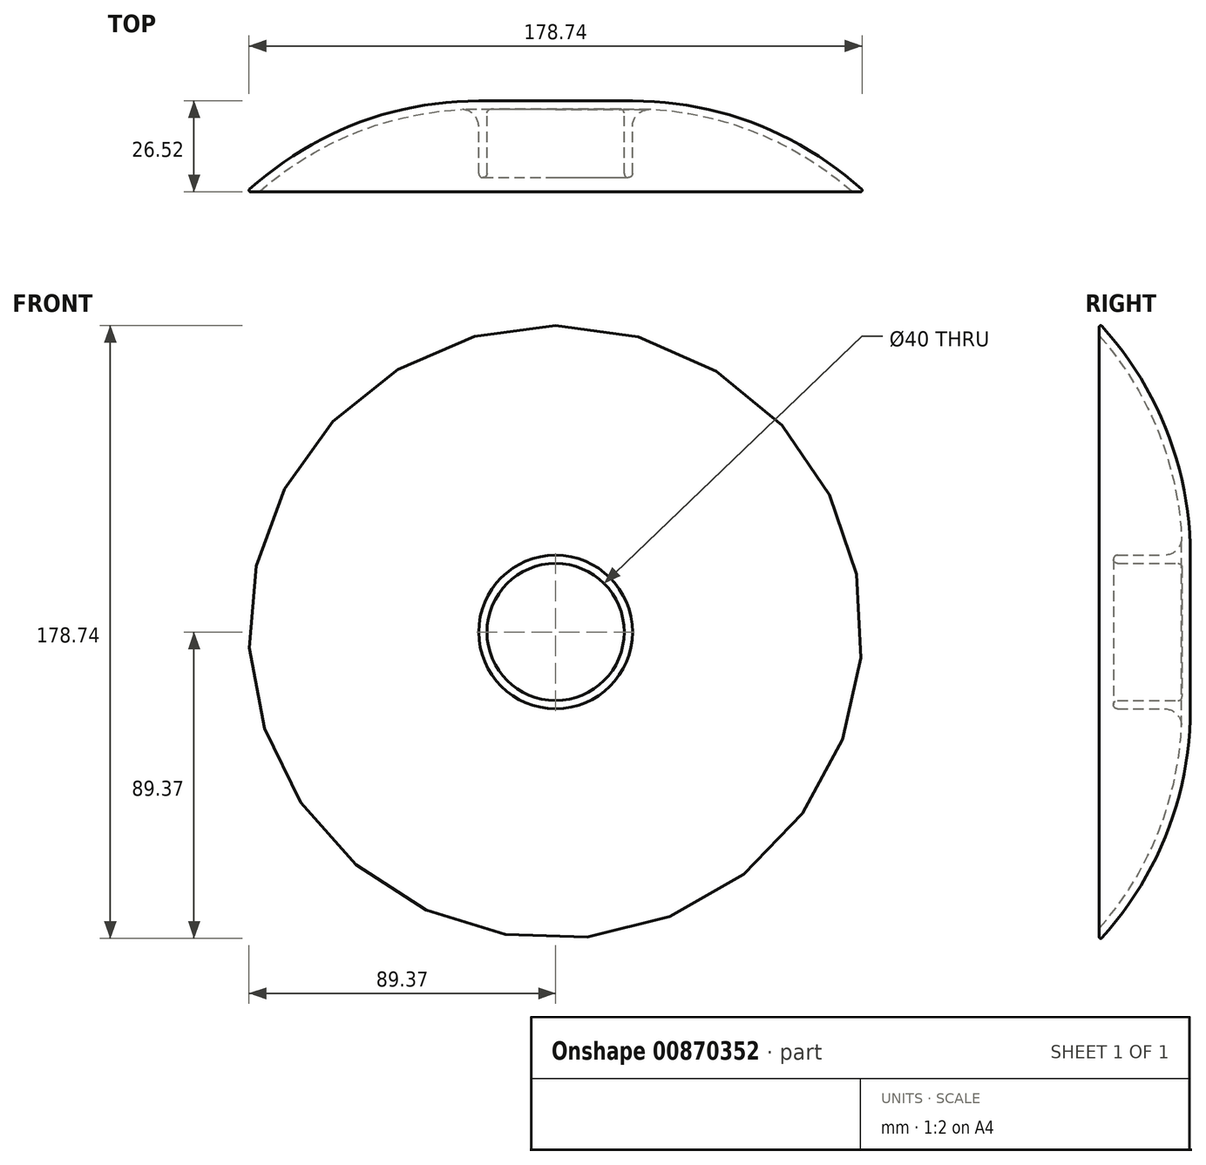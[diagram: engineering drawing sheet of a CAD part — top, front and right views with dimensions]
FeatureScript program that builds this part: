
annotation { "Feature Type Name" : "Feature", "Feature Type Description" : "" }
export const myFeature = defineFeature(function(context is Context, id is Id, definition is map)
    precondition{}
    {
        {
            var Q0;
            Q0=qCreatedBy(makeId("Top.planeOp"),FACE);
            var sketch = newSketch(context, id + "F0", { "sketchPlane" : qUnion([Q0])});
            skLineSegment(sketch, "E0.bottom", {"start": v(0, 32.73) * mm, "end": v(22.4, 32.73) * mm});
            skLineSegment(sketch, "E0.top", {"start": v(0, 30.33) * mm, "end": v(20, 30.33) * mm});
            skArc(sketch, "E1", {"start": v(22.4, 30.33) * mm, "mid": v(56.6, 24.1) * mm, "end": v(86.42, 6.2) * mm});
            skArc(sketch, "E2.0", {"start": v(22.4, 32.73) * mm, "mid": v(58.7, 25.86) * mm, "end": v(90, 6.2) * mm});
            skLineSegment(sketch, "E3", {"start": v(86.42, 6.2) * mm, "end": v(90, 6.2) * mm});
            skLineSegment(sketch, "E4.top", {"start": v(22.4, 10.33) * mm, "end": v(20, 10.33) * mm});
            skLineSegment(sketch, "E4.left", {"start": v(22.4, 30.33) * mm, "end": v(22.4, 10.33) * mm});
            skLineSegment(sketch, "E4.right", {"start": v(20, 30.33) * mm, "end": v(20, 10.33) * mm});
            skLineSegment(sketch, "E5", {"start": v(0, 47.87) * mm, "end": v(0, 16.24) * mm, "construction": true});
            skLineSegment(sketch, "E6", {"start": v(0, 32.73) * mm, "end": v(0, 30.33) * mm});
            skSolve(sketch);
        }
        {
            var Q0;
            Q0 = qSketchRegion(id + "F0", true);
            var Q1;
            Q1=sQuery(id+"F0.wireOp",EDGE,"E5");
            revolve(context, id + "F1", {"surfaceOperationType" : NewSurfaceOperationType.NEW, "entities" : qUnion([Q0]), "axis" : qUnion([Q1]), "revolveType" : RevolveType.FULL});
        }
        {
            var Q0;
            Q0=makeQuery(id+"F1.opRevolve","SWEPT_EDGE",EDGE,{"disambiguationData":[OSD([sQuery(id+"F0.wireOp",EDGE,"E1"),sQuery(id+"F0.wireOp",EDGE,"E4.left")])]});
            fillet(context, id + "F2", {"entities" : qUnion([Q0]), "radius" : 5 * mm, "tangentPropagation" : true, "allowEdgeOverflow" : false});
        }
        {
            var Q0;
            Q0=makeQuery(id+"F1.opRevolve","SWEPT_EDGE",EDGE,{"disambiguationData":[OSD([sQuery(id+"F0.wireOp",EDGE,"E0.top"),sQuery(id+"F0.wireOp",EDGE,"E4.right")])]});
            fillet(context, id + "F3", {"entities" : qUnion([Q0]), "radius" : 1.2 * mm, "tangentPropagation" : true, "allowEdgeOverflow" : false});
        }
        {
            var Q0;
            Q0=makeQuery(id+"F1.opRevolve","SWEPT_EDGE",EDGE,{"disambiguationData":[OSD([sQuery(id+"F0.wireOp",EDGE,"E4.top"),sQuery(id+"F0.wireOp",EDGE,"E4.right")])]});
            var Q1;
            Q1=makeQuery(id+"F1.opRevolve","SWEPT_EDGE",EDGE,{"disambiguationData":[OSD([sQuery(id+"F0.wireOp",EDGE,"E4.top"),sQuery(id+"F0.wireOp",EDGE,"E4.left")])]});
            fillet(context, id + "F4", {"entities" : qUnion([Q0, Q1]), "radius" : 1.2 * mm, "tangentPropagation" : true, "allowEdgeOverflow" : false});
        }
        {
            var Q0;
            Q0=makeQuery(id+"F1.opRevolve","SWEPT_EDGE",EDGE,{"disambiguationData":[OSD([sQuery(id+"F0.wireOp",EDGE,"E2.0"),sQuery(id+"F0.wireOp",EDGE,"E3")])]});
            var Q1;
            Q1=makeQuery(id+"F1.opRevolve","SWEPT_EDGE",EDGE,{"disambiguationData":[OSD([sQuery(id+"F0.wireOp",EDGE,"E1"),sQuery(id+"F0.wireOp",EDGE,"E3")])]});
            fillet(context, id + "F5", {"entities" : qUnion([Q0, Q1]), "radius" : 0.4 * mm, "tangentPropagation" : true, "allowEdgeOverflow" : false});
        }
    });
